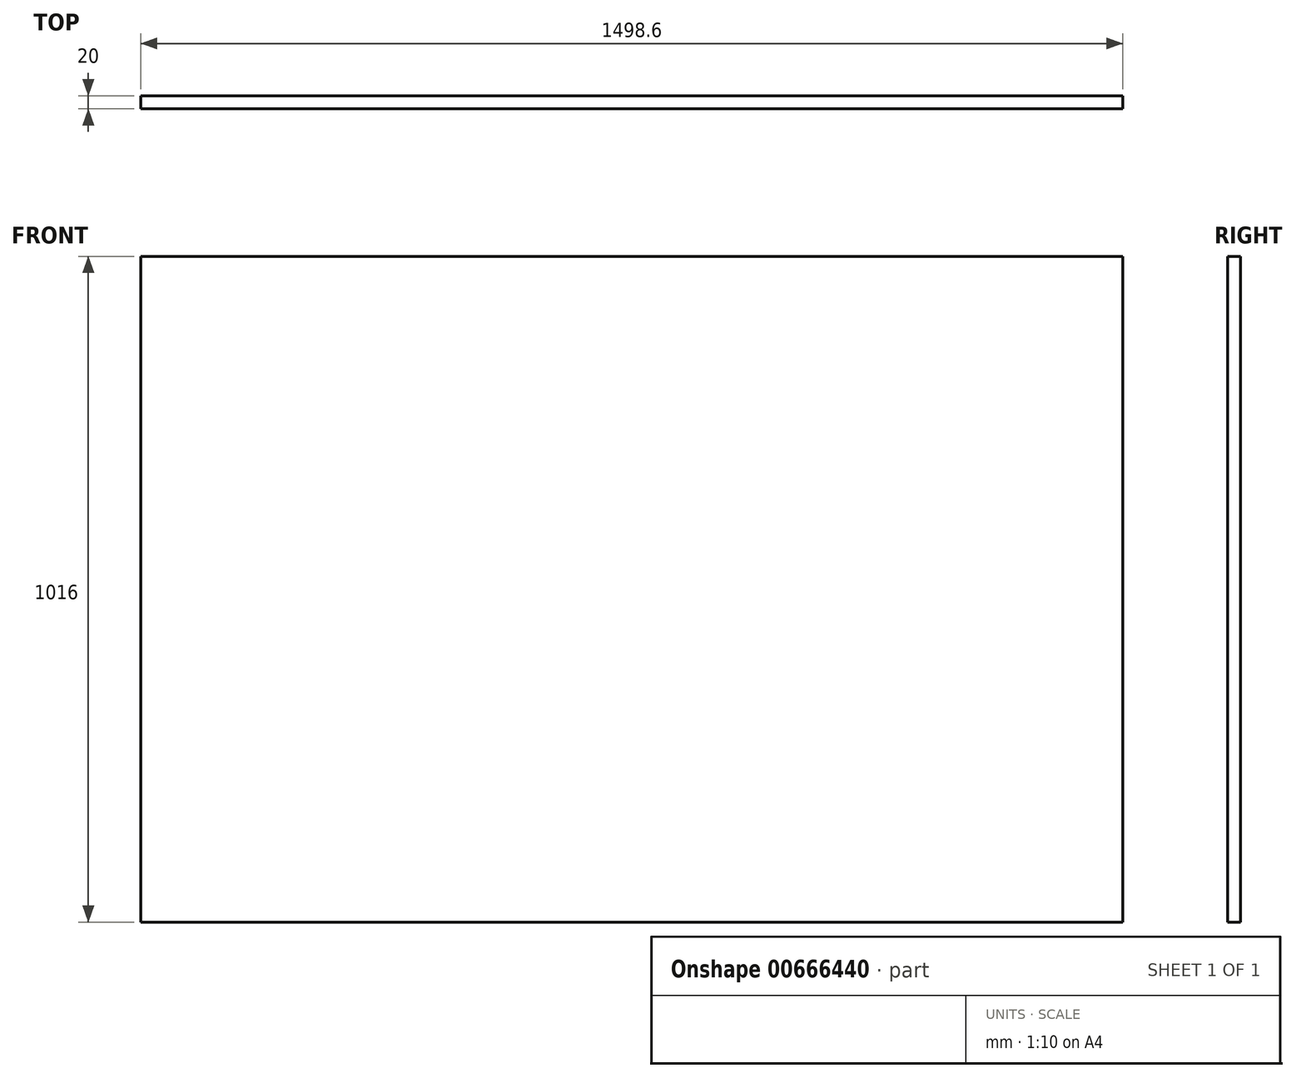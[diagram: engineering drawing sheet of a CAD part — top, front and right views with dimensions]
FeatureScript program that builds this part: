
annotation { "Feature Type Name" : "Feature", "Feature Type Description" : "" }
export const myFeature = defineFeature(function(context is Context, id is Id, definition is map)
    precondition{}
    {
        {
            var Q0;
            Q0=qCreatedBy(makeId("Front.planeOp"),FACE);
            var sketch = newSketch(context, id + "F0", { "sketchPlane" : qUnion([Q0])});
            skLineSegment(sketch, "E0.bottom", {"start": v(749.3, 508) * mm, "end": v(-749.3, 508) * mm});
            skLineSegment(sketch, "E0.top", {"start": v(749.3, -508) * mm, "end": v(-749.3, -508) * mm});
            skLineSegment(sketch, "E0.left", {"start": v(749.3, 508) * mm, "end": v(749.3, -508) * mm});
            skLineSegment(sketch, "E0.right", {"start": v(-749.3, 508) * mm, "end": v(-749.3, -508) * mm});
            skPoint(sketch, "E0.middle", {"position": v(0, 0) * mm});
            skSolve(sketch);
        }
        {
            var Q0;
            Q0 = qSketchRegion(id + "F0", true);
            extrude(context, id + "F1", {"entities" : qUnion([Q0]), "depth" : 20 * mm, "offsetDistance" : 25.4 * mm});
        }
    });
